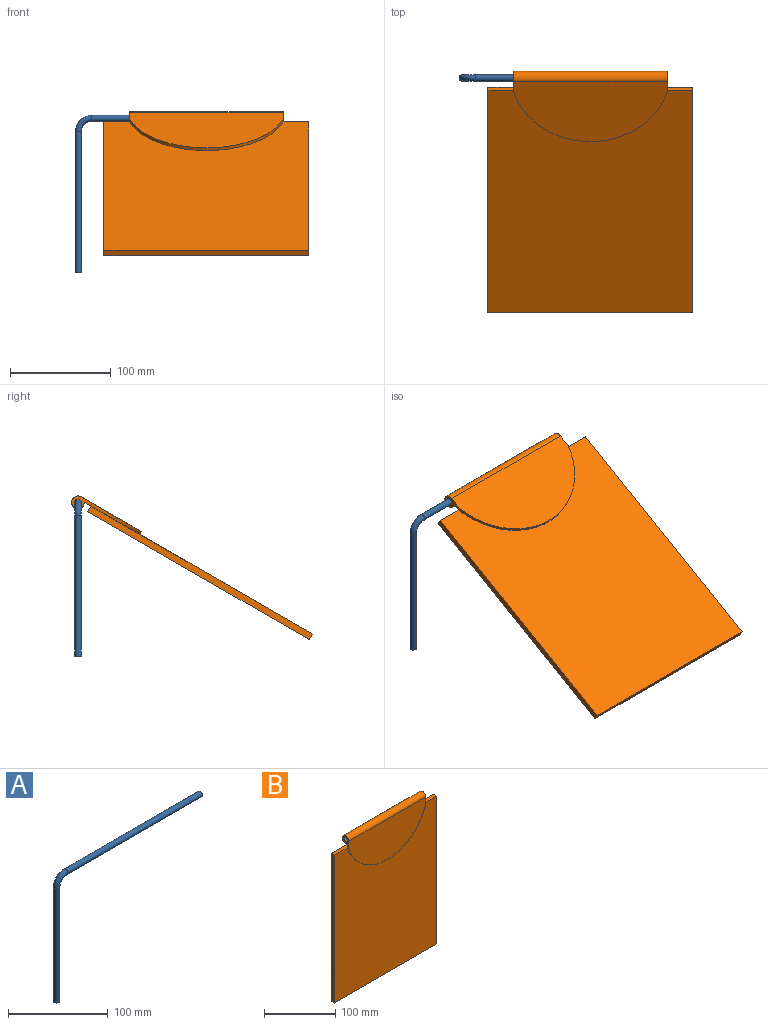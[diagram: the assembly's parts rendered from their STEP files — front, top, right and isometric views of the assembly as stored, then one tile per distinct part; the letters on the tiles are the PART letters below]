
ASSEMBLY  parts=2 mates=1
PART A: 5 faces, bbox 207.7x6.4x156.9 mm
  f0: cylinder r=3.17mm len=190.5mm, axis (1,0,0), area 3800.3mm2, adj f1,f2
  f1: plane 6.35x6.35mm, normal (1,0,0), area 31.7mm2, adj f0
  f2: torus R=12.7mm, axis (0,1,0), area 398mm2, adj f0,f3
  f3: cylinder r=3.17mm len=139.7mm, axis (0,0,1), area 2786.9mm2, adj f2,f4
  f4: plane 6.35x6.35mm, normal (0,0,-1), area 31.7mm2, adj f3
PART B: 13 faces, bbox 203.2x12.7x273.1 mm
  f0: plane 203.2x6.35mm, normal (0,0,-1), area 1290.3mm2, adj f1,f3,f4,f5
  f1: plane 254x6.35mm, normal (1,0,0), area 1612.9mm2, adj f0,f2,f4,f5
  f2: plane 203.2x6.35mm, normal (0,0,1), area 1290.3mm2, adj f1,f3,f4,f5,f6
  f3: plane 254x6.35mm, normal (-1,0,0), area 1612.9mm2, adj f0,f2,f4,f5
  f4: plane 254x203.2mm, normal (0,1,0), area 51612.8mm2, adj f0,f1,f2,f3
  f5: plane 254x203.2mm, normal (0,-1,0), area 45254.8mm2, adj f0,f1,f2,f3,f8
  f6: plane 152.4x7.2mm, normal (0,1,0), area 1097.4mm2, adj f2,f7,f9,f11
  f7: plane 19.05x12.7mm, normal (-1,0,0), area 122.9mm2, adj f6,f8,f10,f11,f12
  f8: cylinder r=79.55mm len=152.4mm, axis (0,1,0), area 646.4mm2, adj f5,f7,f9,f10
  f9: plane 19.05x12.7mm, normal (1,0,0), area 122.9mm2, adj f6,f8,f10,f11,f12
  f10: plane 152.4x69.42mm, normal (0,-1,0), area 8293.5mm2, adj f7,f8,f9,f11
  f11: cylinder r=6.35mm len=152.4mm, axis (-1,0,0), area 5067.1mm2, adj f6,f7,f9,f10
  f12: cylinder r=3.17mm len=152.4mm, axis (-1,0,0), area 3040.2mm2, adj f7,f9
PLACE A t=(-1190.58,-234.63,703.96)mm
PLACE B rot(axis=(-1,0,0),60deg) t=(-1063.58,-357.21,789.26)mm
MATE revolute B.f11 <-> A.f0  axis (-1,0,0) through (-987.38,-234.63,856.36)mm
